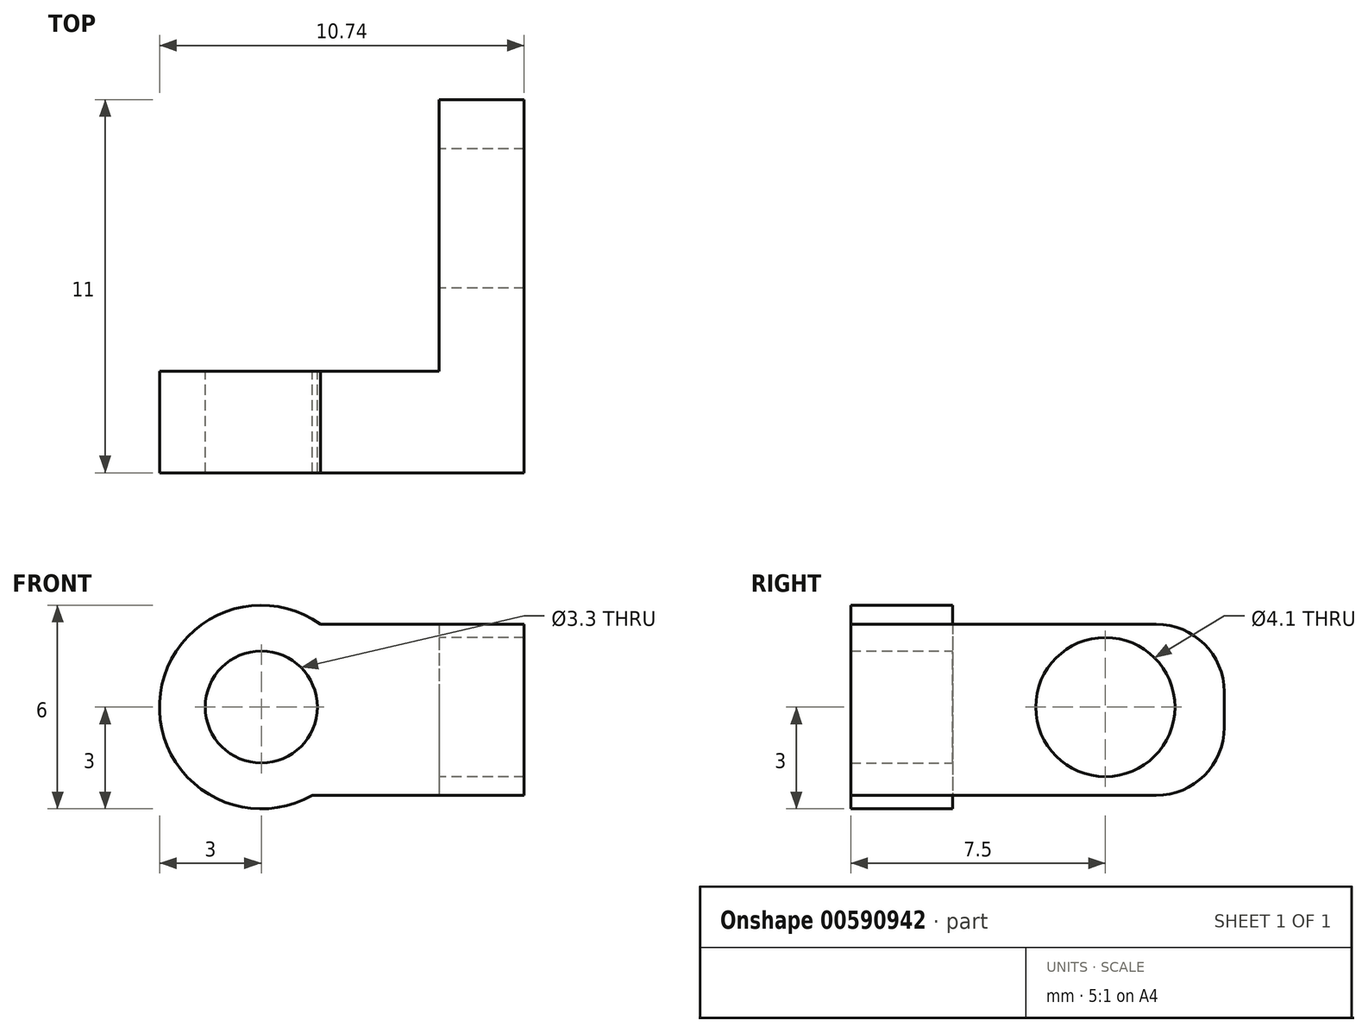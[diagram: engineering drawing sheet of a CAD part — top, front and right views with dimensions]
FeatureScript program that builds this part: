
annotation { "Feature Type Name" : "Feature", "Feature Type Description" : "" }
export const myFeature = defineFeature(function(context is Context, id is Id, definition is map)
    precondition{}
    {
        {
            var Q0;
            Q0=qCreatedBy(makeId("Front.planeOp"),FACE);
            var sketch = newSketch(context, id + "F0", { "sketchPlane" : qUnion([Q0])});
            skCircle(sketch, "E0", {"center": v(0, 0) * mm, "radius": 1.65 * mm});
            skCircle(sketch, "E1.0", {"center": v(0, 0) * mm, "radius": 3 * mm});
            skSolve(sketch);
        }
        {
            var Q0;
            Q0=qSketchRegion(id+"F0",true);
            extrude(context, id + "F1", {"entities" : qUnion([Q0]), "depth" : 1.5 * mm, "offsetDistance" : 25 * mm, "hasSecondDirection" : true, "secondDirectionOppositeDirection" : true, "secondDirectionDepth" : 1.5 * mm});
        }
        {
            var Q0;
            Q0=qCreatedBy(makeId("Front.planeOp"),FACE);
            var sketch = newSketch(context, id + "F2", { "sketchPlane" : qUnion([Q0])});
            skLineSegment(sketch, "E2", {"start": v(1.74, 2.44) * mm, "end": v(7.74, 2.44) * mm});
            skLineSegment(sketch, "E3", {"start": v(7.74, 2.44) * mm, "end": v(7.74, -2.6) * mm});
            skLineSegment(sketch, "E4", {"start": v(7.74, -2.6) * mm, "end": v(1.5, -2.6) * mm});
            skCircle(sketch, "E5.3", {"center": v(0, 0) * mm, "radius": 3 * mm});
            skSolve(sketch);
        }
        {
            var Q0;
            {var subQ0=sQuery(id+"F2.wireOp",EDGE,"E2");Q0=makeQuery(id+"F2.imprint","IMPRINT",FACE,{"disambiguationData":[TD([[makeQuery(id+"F2.imprint","IMPRINT",EDGE,{"derivedFrom":subQ0}),-1.0]])]});}
            extrude(context, id + "F3", {"entities" : qUnion([Q0]), "operationType" : NewBodyOperationType.ADD, "depth" : 1.5 * mm, "offsetDistance" : 25 * mm, "hasSecondDirection" : true, "secondDirectionOppositeDirection" : true, "secondDirectionDepth" : 1.5 * mm});
        }
        {
            var Q0;
            Q0=makeQuery(id+"F3.boolean.opBoolean","MERGE",FACE,{"derivedFrom":[makeQuery(id+"F1.opExtrude","CAP_FACE",FACE,{"disambiguationData":[OSD([sQuery(id+"F0.wireOp",EDGE,"E0"),sQuery(id+"F0.wireOp",EDGE,"E1.0")])],"isStart":true}),makeQuery(id+"F3.opExtrude","CAP_FACE",FACE,{"disambiguationData":[OSD([sQuery(id+"F2.wireOp",EDGE,"E2"),sQuery(id+"F2.wireOp",EDGE,"E3"),sQuery(id+"F2.wireOp",EDGE,"E4"),sQuery(id+"F2.wireOp",EDGE,"E5.3")])],"isStart":true})]});
            var sketch = newSketch(context, id + "F4", { "sketchPlane" : qUnion([Q0])});
            skLineSegment(sketch, "E6.bottom", {"start": v(-7.74, 2.44) * mm, "end": v(-5.24, 2.44) * mm});
            skLineSegment(sketch, "E6.top", {"start": v(-7.74, -2.6) * mm, "end": v(-5.24, -2.6) * mm});
            skLineSegment(sketch, "E6.left", {"start": v(-7.74, 2.44) * mm, "end": v(-7.74, -2.6) * mm});
            skLineSegment(sketch, "E6.right", {"start": v(-5.24, 2.44) * mm, "end": v(-5.24, -2.6) * mm});
            skSolve(sketch);
        }
        {
            var Q0;
            Q0=makeQuery(id+"F4.imprint","IMPRINT",FACE,{"disambiguationData":[TD([[makeQuery(id+"F4.imprint","IMPRINT",EDGE,{"derivedFrom":sQuery(id+"F4.wireOp",EDGE,"E6.bottom")}),1.0]])]});
            extrude(context, id + "F5", {"entities" : qUnion([Q0]), "operationType" : NewBodyOperationType.ADD, "depth" : 8 * mm, "offsetDistance" : 25 * mm});
        }
        {
            var Q0;
            Q0=makeQuery(id+"F5.opExtrude","SWEPT_FACE",FACE,{"disambiguationData":[OSD([sQuery(id+"F4.wireOp",EDGE,"E6.right")])]});
            var sketch = newSketch(context, id + "F6", { "sketchPlane" : qUnion([Q0])});
            skCircle(sketch, "E7", {"center": v(-6, 0) * mm, "radius": 2.05 * mm});
            skSolve(sketch);
        }
        {
            var Q0;
            Q0=makeQuery(id+"F6.imprint","IMPRINT",FACE,{"disambiguationData":[TD([[makeQuery(id+"F6.imprint","IMPRINT",EDGE,{"derivedFrom":sQuery(id+"F6.wireOp",EDGE,"E7")}),1.0]])]});
            extrude(context, id + "F7", {"entities" : qUnion([Q0]), "operationType" : NewBodyOperationType.REMOVE, "oppositeDirection" : true, "depth" : 25 * mm, "offsetDistance" : 25 * mm});
        }
        {
            var Q0;
            Q0=makeQuery(id+"F5.opExtrude","CAP_EDGE",EDGE,{"disambiguationData":[OSD([sQuery(id+"F4.wireOp",EDGE,"E6.top")])],"isStart":false});
            var Q1;
            Q1=makeQuery(id+"F5.opExtrude","CAP_EDGE",EDGE,{"disambiguationData":[OSD([sQuery(id+"F4.wireOp",EDGE,"E6.bottom")])],"isStart":false});
            fillet(context, id + "F8", {"entities" : qUnion([Q0, Q1]), "radius" : 2 * mm, "tangentPropagation" : true, "allowEdgeOverflow" : false});
        }
    });
